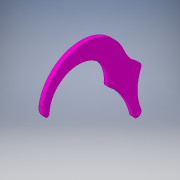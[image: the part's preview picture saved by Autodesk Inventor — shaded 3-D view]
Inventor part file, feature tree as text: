
AUTODESK INVENTOR PART (.ipt)
format: ipt  version: 2017 SP1 (Build 210196100, 196)  size: 144,896 bytes
history: native  units: in
note: dims shown in document units (in); Inventor stores cm internally (conversion verified against a paired STEP export)
features: extrude x1, fillet x1, sketch x1
ambient origin geometry x8: Origin, YZ Plane, XZ Plane, XY Plane, X Axis, Y Axis, Z Axis, Center Point
bodies: Solid1 (feature_tree)
feature tree (3):
  extrude  "Extrusion1"  Depth=0.125in
  fillet  "Fillet2"  Radius=0.25in
  sketch  "Sketch1"  dims[d0=2.5in d1=1.625in d2=0.25in d4=0.25in d6=3.75in d8=0.1875in d9=0.75in d10=0.25in d12=1.25in d14=0.25in d15=0.0in d21=2.0in d24=0.02in d25=0.125in]
